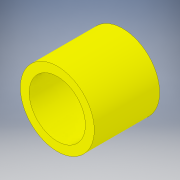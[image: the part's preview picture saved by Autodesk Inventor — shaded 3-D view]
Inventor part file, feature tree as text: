
AUTODESK INVENTOR PART (.ipt)
format: ipt  version: 2018.2 (Build 222227000, 227)  size: 111,104 bytes
history: native  units: in
note: dims shown in document units (in); Inventor stores cm internally (conversion verified against a paired STEP export)
features: extrude x1, sketch x1
ambient origin geometry x8: Origin, YZ Plane, XZ Plane, XY Plane, X Axis, Y Axis, Z Axis, Center Point
bodies: Solid1 (feature_tree)
feature tree (2):
  extrude  "Extrusion1"  Depth=1.163in
  sketch  "Sketch1"  dims[d0=1.315in d1=1.0in d2=1.163in d3=0.0in]
